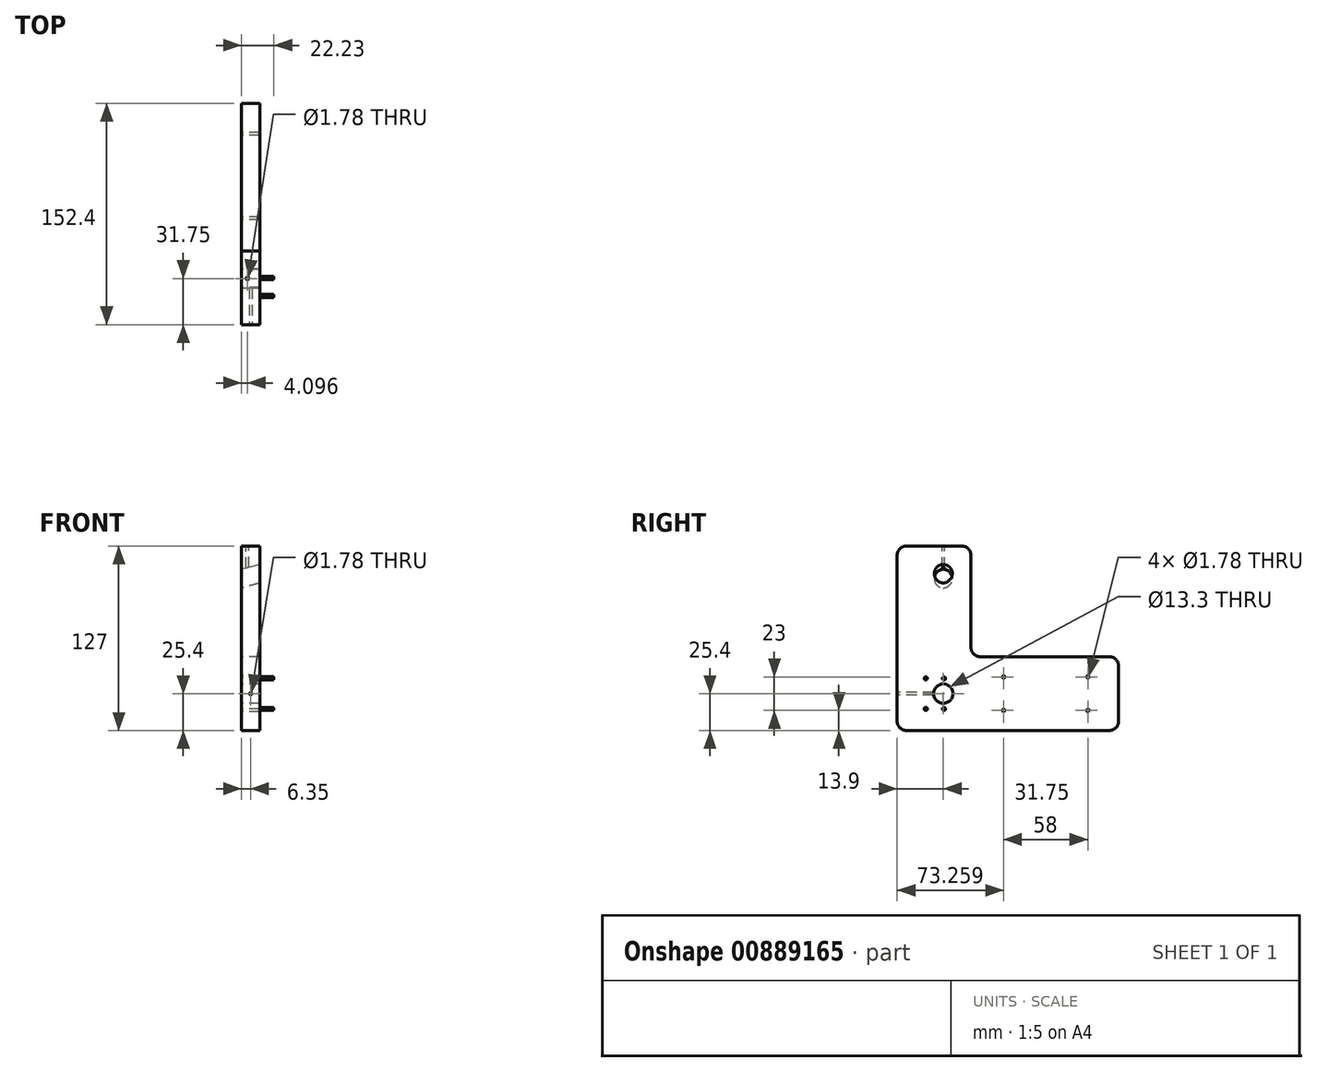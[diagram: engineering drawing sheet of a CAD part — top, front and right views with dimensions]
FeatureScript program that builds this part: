
annotation { "Feature Type Name" : "Feature", "Feature Type Description" : "" }
export const myFeature = defineFeature(function(context is Context, id is Id, definition is map)
    precondition{}
    {
        {
            var Q0;
            Q0=qCreatedBy(makeId("Right.planeOp"),FACE);
            var sketch = newSketch(context, id + "F0", { "sketchPlane" : qUnion([Q0])});
            skLineSegment(sketch, "E0", {"start": v(-50.8, 76.2) * mm, "end": v(-50.8, -50.8) * mm});
            skLineSegment(sketch, "E1", {"start": v(-50.8, -50.8) * mm, "end": v(101.6, -50.8) * mm});
            skLineSegment(sketch, "E2", {"start": v(101.6, -50.8) * mm, "end": v(101.6, 0) * mm});
            skLineSegment(sketch, "E3", {"start": v(101.6, 0) * mm, "end": v(0, 0) * mm});
            skLineSegment(sketch, "E4", {"start": v(0, 0) * mm, "end": v(0, 76.2) * mm});
            skLineSegment(sketch, "E5", {"start": v(0, 76.2) * mm, "end": v(-50.8, 76.2) * mm});
            skCircle(sketch, "E6", {"center": v(-19.05, -25.4) * mm, "radius": 6.65 * mm});
            skLineSegment(sketch, "E7", {"start": v(-19.05, -25.4) * mm, "end": v(-19.05, 53.79) * mm, "construction": true});
            skLineSegment(sketch, "E8", {"start": v(114, -25.4) * mm, "end": v(-89.2, -25.4) * mm, "construction": true});
            skLineSegment(sketch, "E9", {"start": v(22.46, -13.9) * mm, "end": v(80.46, -13.9) * mm, "construction": true});
            skCircle(sketch, "E10", {"center": v(22.46, -13.9) * mm, "radius": 0.89 * mm});
            skCircle(sketch, "E11", {"center": v(80.46, -13.9) * mm, "radius": 0.89 * mm});
            skCircle(sketch, "E12.MirrorC", {"center": v(22.46, -36.9) * mm, "radius": 0.89 * mm});
            skLineSegment(sketch, "E13.MirrorCS", {"start": v(22.46, -36.9) * mm, "end": v(80.46, -36.9) * mm, "construction": true});
            skCircle(sketch, "E14.MirrorC", {"center": v(80.46, -36.9) * mm, "radius": 0.89 * mm});
            skLineSegment(sketch, "E15", {"start": v(6.8, -14.9) * mm, "end": v(-59.4, -14.9) * mm, "construction": true});
            skCircle(sketch, "E16", {"center": v(-18.59, -14.9) * mm, "radius": 1.07 * mm, "construction": true});
            skCircle(sketch, "E17", {"center": v(-31.09, -14.9) * mm, "radius": 1.07 * mm, "construction": true});
            skLineSegment(sketch, "E18.MirrorCS", {"start": v(6.8, -35.9) * mm, "end": v(-59.4, -35.9) * mm, "construction": true});
            skCircle(sketch, "E19.MirrorC", {"center": v(-31.09, -35.9) * mm, "radius": 1.07 * mm, "construction": true});
            skCircle(sketch, "E20.MirrorC", {"center": v(-18.59, -35.9) * mm, "radius": 1.07 * mm, "construction": true});
            skSolve(sketch);
        }
        {
            var Q0;
            Q0 = qSketchRegion(id + "F0", true);
            extrude(context, id + "F1", {"entities" : qUnion([Q0]), "depth" : 12.7 * mm, "offsetDistance" : 25.4 * mm});
        }
        {
            var Q0;
            Q0=makeQuery(id+"F1.opExtrude","CAP_FACE",FACE,{"disambiguationData":[OSD([sQuery(id+"F0.wireOp",EDGE,"E0"),sQuery(id+"F0.wireOp",EDGE,"E1"),sQuery(id+"F0.wireOp",EDGE,"E2"),sQuery(id+"F0.wireOp",EDGE,"E3"),sQuery(id+"F0.wireOp",EDGE,"E4"),sQuery(id+"F0.wireOp",EDGE,"E5"),sQuery(id+"F0.wireOp",EDGE,"E10"),sQuery(id+"F0.wireOp",EDGE,"E11"),sQuery(id+"F0.wireOp",EDGE,"E12.MirrorC"),sQuery(id+"F0.wireOp",EDGE,"E14.MirrorC")])],"isStart":false});
            var sketch = newSketch(context, id + "F2", { "sketchPlane" : qUnion([Q0])});
            skCircle(sketch, "E21.0", {"center": v(-31.09, -14.9) * mm, "radius": 1.07 * mm});
            skCircle(sketch, "E21.1", {"center": v(-18.59, -14.9) * mm, "radius": 1.07 * mm});
            skCircle(sketch, "E21.2", {"center": v(-18.59, -35.9) * mm, "radius": 1.07 * mm});
            skCircle(sketch, "E21.3", {"center": v(-31.09, -35.9) * mm, "radius": 1.07 * mm});
            skSolve(sketch);
        }
        {
            var Q0;
            Q0 = qSketchRegion(id + "F2", true);
            extrude(context, id + "F3", {"entities" : qUnion([Q0]), "operationType" : NewBodyOperationType.ADD, "depth" : 9.52 * mm, "offsetDistance" : 25.4 * mm});
        }
        {
            var Q0;
            Q0=makeQuery(id+"F1.opExtrude","SWEPT_EDGE",EDGE,{"disambiguationData":[OSD([sQuery(id+"F0.wireOp",EDGE,"E3"),sQuery(id+"F0.wireOp",EDGE,"E4")])]});
            fillet(context, id + "F4", {"entities" : qUnion([Q0]), "radius" : 6.35 * mm, "tangentPropagation" : true, "allowEdgeOverflow" : false});
        }
        {
            var Q0;
            Q0=makeQuery(id+"F1.opExtrude","SWEPT_EDGE",EDGE,{"disambiguationData":[OSD([sQuery(id+"F0.wireOp",EDGE,"E0"),sQuery(id+"F0.wireOp",EDGE,"E1")])]});
            var Q1;
            Q1=makeQuery(id+"F1.opExtrude","SWEPT_EDGE",EDGE,{"disambiguationData":[OSD([sQuery(id+"F0.wireOp",EDGE,"E0"),sQuery(id+"F0.wireOp",EDGE,"E5")])]});
            var Q2;
            Q2=makeQuery(id+"F1.opExtrude","SWEPT_EDGE",EDGE,{"disambiguationData":[OSD([sQuery(id+"F0.wireOp",EDGE,"E1"),sQuery(id+"F0.wireOp",EDGE,"E2")])]});
            fillet(context, id + "F5", {"entities" : qUnion([Q0, Q1, Q2]), "radius" : 6.35 * mm, "tangentPropagation" : true, "allowEdgeOverflow" : false});
        }
        {
            var Q0;
            Q0=makeQuery(id+"F1.opExtrude","SWEPT_EDGE",EDGE,{"disambiguationData":[OSD([sQuery(id+"F0.wireOp",EDGE,"E4"),sQuery(id+"F0.wireOp",EDGE,"E5")])]});
            var Q1;
            Q1=makeQuery(id+"F1.opExtrude","SWEPT_EDGE",EDGE,{"disambiguationData":[OSD([sQuery(id+"F0.wireOp",EDGE,"E2"),sQuery(id+"F0.wireOp",EDGE,"E3")])]});
            fillet(context, id + "F6", {"entities" : qUnion([Q0, Q1]), "radius" : 6.35 * mm, "tangentPropagation" : true, "allowEdgeOverflow" : false});
        }
        {
            var Q0;
            Q0=makeQuery(id+"F1.opExtrude","CAP_FACE",FACE,{"disambiguationData":[OSD([sQuery(id+"F0.wireOp",EDGE,"E0"),sQuery(id+"F0.wireOp",EDGE,"E1"),sQuery(id+"F0.wireOp",EDGE,"E2"),sQuery(id+"F0.wireOp",EDGE,"E3"),sQuery(id+"F0.wireOp",EDGE,"E4"),sQuery(id+"F0.wireOp",EDGE,"E5"),sQuery(id+"F0.wireOp",EDGE,"E6"),sQuery(id+"F0.wireOp",EDGE,"E10"),sQuery(id+"F0.wireOp",EDGE,"E11"),sQuery(id+"F0.wireOp",EDGE,"E12.MirrorC"),sQuery(id+"F0.wireOp",EDGE,"E14.MirrorC")])],"isStart":false});
            var sketch = newSketch(context, id + "F7", { "sketchPlane" : qUnion([Q0])});
            skLineSegment(sketch, "E22.0", {"start": v(-19.05, -25.4) * mm, "end": v(-19.05, 53.79) * mm, "construction": true});
            skLineSegment(sketch, "E23", {"start": v(-19.05, 53.79) * mm, "end": v(-19.05, 72.49) * mm, "construction": true});
            skSolve(sketch);
        }
        {
            var Q0;
            Q0=sQuery(id+"F7.wireOp",VERTEX,"E23.end");
            var Q1;
            Q1=sQuery(id+"F0.wireOp",VERTEX,"E7.end");
            var Q2;
            Q2=sQuery(id+"F7.wireOp",VERTEX,"E22.0.end");
            cPlane(context, id + "F8", {"entities" : qUnion([Q0, Q1, Q2]), "cplaneType" : CPlaneType.THREE_POINT, "offset" : 25.4 * mm, "width" : 152.4 * mm, "height" : 152.4 * mm});
        }
        {
            var Q0;
            Q0=qCreatedBy(id+"F8.planeOp",FACE);
            var sketch = newSketch(context, id + "F9", { "sketchPlane" : qUnion([Q0])});
            skPoint(sketch, "E24.0", {"position": v(0, 53.79) * mm});
            skPoint(sketch, "E24.1", {"position": v(-12.7, 72.49) * mm});
            skLineSegment(sketch, "E25", {"start": v(69.46, 35.17) * mm, "end": v(-53.2, 68.04) * mm});
            skSolve(sketch);
        }
        {
            var Q0;
            Q0=sQuery(id+"F9.wireOp",VERTEX,"E24.1");
            var Q1;
            Q1=sQuery(id+"F9.wireOp",EDGE,"E25");
            cPlane(context, id + "F10", {"entities" : qUnion([Q0, Q1]), "cplaneType" : CPlaneType.LINE_POINT, "offset" : 25.4 * mm, "width" : 152.4 * mm, "height" : 152.4 * mm});
        }
        {
            var Q0;
            Q0=qCreatedBy(id+"F10.planeOp",FACE);
            var Q1;
            Q1=sQuery(id+"F9.wireOp",VERTEX,"E25.end");
            cPlane(context, id + "F11", {"entities" : qUnion([Q0, Q1]), "cplaneType" : CPlaneType.PLANE_POINT, "offset" : 25.4 * mm, "width" : 152.4 * mm, "height" : 152.4 * mm});
        }
        {
            var Q0;
            Q0=qCreatedBy(id+"F11.planeOp",FACE);
            var sketch = newSketch(context, id + "F12", { "sketchPlane" : qUnion([Q0])});
            skPoint(sketch, "E26.0", {"position": v(-19.05, 51.95) * mm});
            skCircle(sketch, "E27", {"center": v(-19.05, 51.95) * mm, "radius": 6.15 * mm});
            skSolve(sketch);
        }
        {
            var Q0;
            Q0=makeQuery(id+"F12.imprint","IMPRINT",FACE,{"disambiguationData":[TD([[makeQuery(id+"F12.imprint","IMPRINT",EDGE,{"derivedFrom":sQuery(id+"F12.wireOp",EDGE,"E27")}),1.0]])]});
            var Q1;
            Q1 = qConstructionFilter(qBodyType(qCreatedBy(id + "F9" ,EDGE), BodyType.WIRE), ConstructionObject.NO);
            sweep(context, id + "F13", {"operationType" : NewBodyOperationType.REMOVE, "profiles" : qUnion([Q0]), "path" : qUnion([Q1])});
        }
        {
            var Q0;
            Q0=makeQuery(id+"F1.opExtrude","SWEPT_FACE",FACE,{"disambiguationData":[OSD([sQuery(id+"F0.wireOp",EDGE,"E5")])]});
            var sketch = newSketch(context, id + "F14", { "sketchPlane" : qUnion([Q0])});
            skPoint(sketch, "E28.1", {"position": v(0, -19.05) * mm});
            skLineSegment(sketch, "E29", {"start": v(0, -19.05) * mm, "end": v(8.2, -19.05) * mm, "construction": true});
            skCircle(sketch, "E30", {"center": v(4.1, -19.05) * mm, "radius": 0.89 * mm});
            skSolve(sketch);
        }
        {
            var Q0;
            Q0 = qSketchRegion(id + "F14", true);
            extrude(context, id + "F15", {"entities" : qUnion([Q0]), "operationType" : NewBodyOperationType.REMOVE, "endBound" : BoundingType.UP_TO_NEXT, "oppositeDirection" : true, "depth" : 25.4 * mm, "offsetDistance" : 25.4 * mm});
        }
        {
            var Q0;
            Q0=makeQuery(id+"F1.opExtrude","SWEPT_FACE",FACE,{"disambiguationData":[OSD([sQuery(id+"F0.wireOp",EDGE,"E0")])]});
            var sketch = newSketch(context, id + "F16", { "sketchPlane" : qUnion([Q0])});
            skPoint(sketch, "E31.0", {"position": v(0, -25.4) * mm});
            skLineSegment(sketch, "E32", {"start": v(0, -25.4) * mm, "end": v(12.7, -25.4) * mm, "construction": true});
            skCircle(sketch, "E33", {"center": v(6.35, -25.4) * mm, "radius": 0.89 * mm});
            skSolve(sketch);
        }
        {
            var Q0;
            Q0 = qSketchRegion(id + "F16", true);
            extrude(context, id + "F17", {"entities" : qUnion([Q0]), "operationType" : NewBodyOperationType.REMOVE, "endBound" : BoundingType.UP_TO_NEXT, "oppositeDirection" : true, "depth" : 25.4 * mm, "offsetDistance" : 25.4 * mm});
        }
    });
